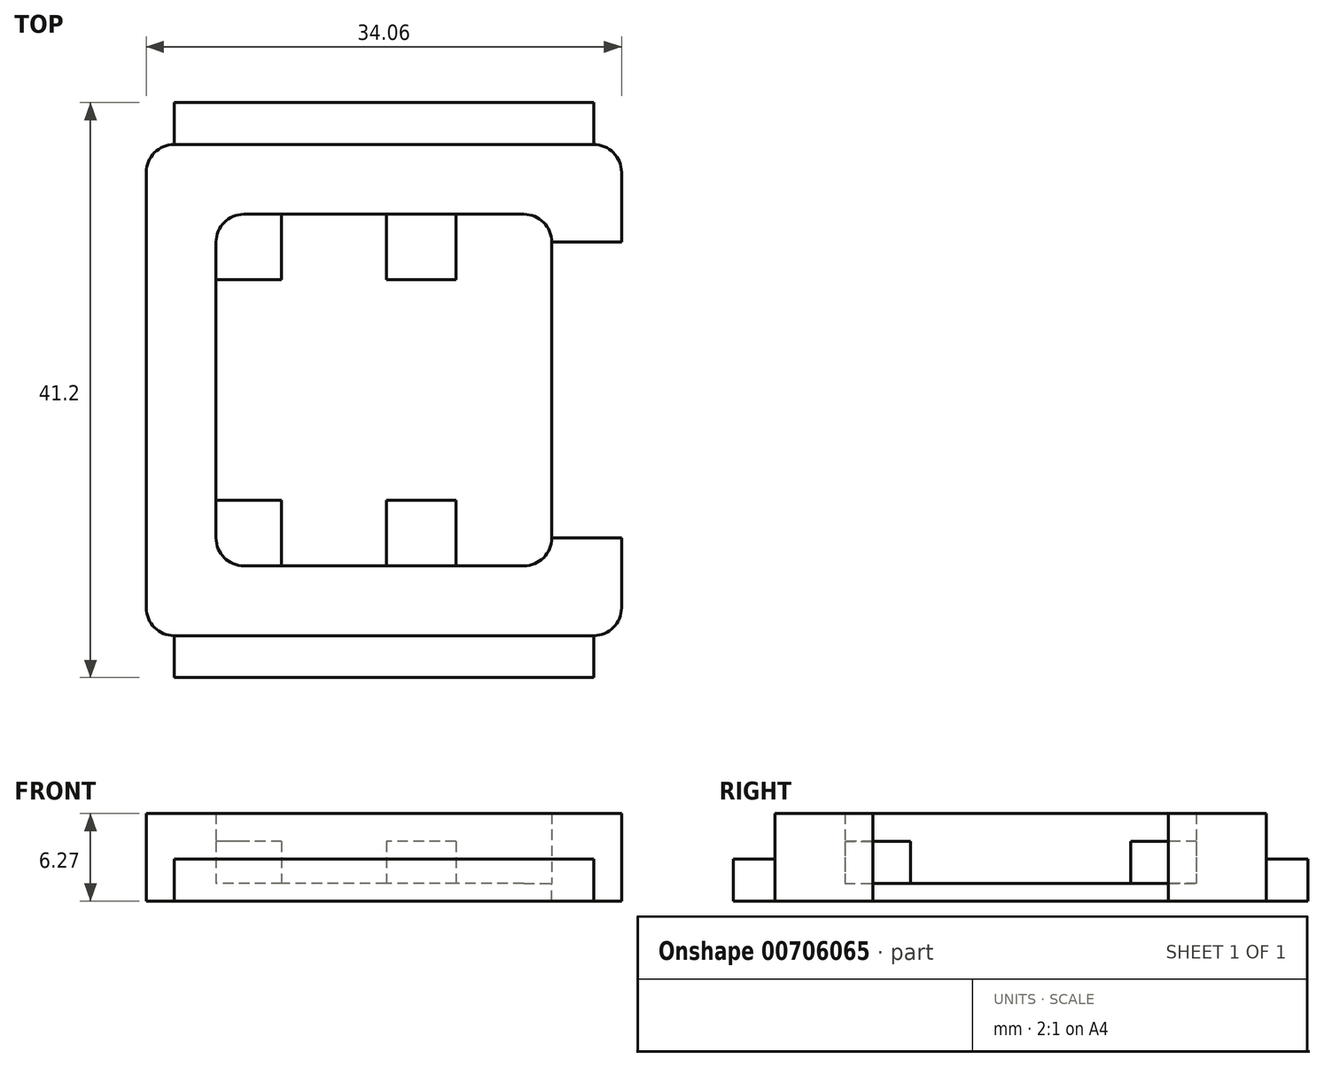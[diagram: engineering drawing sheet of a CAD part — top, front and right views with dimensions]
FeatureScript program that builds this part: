
annotation { "Feature Type Name" : "Feature", "Feature Type Description" : "" }
export const myFeature = defineFeature(function(context is Context, id is Id, definition is map)
    precondition{}
    {
        {
            var Q0;
            Q0=qCreatedBy(makeId("Top.planeOp"),FACE);
            var sketch = newSketch(context, id + "F0", { "sketchPlane" : qUnion([Q0])});
            skLineSegment(sketch, "E0.bottom", {"start": v(10.03, -12.6) * mm, "end": v(-10.03, -12.6) * mm});
            skLineSegment(sketch, "E0.top", {"start": v(10.03, 12.6) * mm, "end": v(-10.03, 12.6) * mm});
            skLineSegment(sketch, "E0.left", {"start": v(12.03, -10.6) * mm, "end": v(12.03, 10.6) * mm});
            skLineSegment(sketch, "E0.right", {"start": v(-12.03, -10.6) * mm, "end": v(-12.03, 10.6) * mm});
            skPoint(sketch, "E0.middle", {"position": v(0, 0) * mm});
            skPoint(sketch, "E1.visualSharp", {"position": v(-12.03, 12.6) * mm});
            skArc(sketch, "E1.filletArc", {"start": v(-10.03, 12.6) * mm, "mid": v(-11.45, 12.01) * mm, "end": v(-12.03, 10.6) * mm});
            skPoint(sketch, "E2.visualSharp", {"position": v(12.03, 12.6) * mm});
            skArc(sketch, "E2.filletArc", {"start": v(12.03, 10.6) * mm, "mid": v(11.45, 12.01) * mm, "end": v(10.03, 12.6) * mm});
            skPoint(sketch, "E3.visualSharp", {"position": v(12.03, -12.6) * mm});
            skArc(sketch, "E3.filletArc", {"start": v(10.03, -12.6) * mm, "mid": v(11.45, -12.01) * mm, "end": v(12.03, -10.6) * mm});
            skPoint(sketch, "E4.visualSharp", {"position": v(-12.03, -12.6) * mm});
            skArc(sketch, "E4.filletArc", {"start": v(-12.03, -10.6) * mm, "mid": v(-11.45, -12.01) * mm, "end": v(-10.03, -12.6) * mm});
            skCircle(sketch, "E5", {"center": v(-10.03, -10.6) * mm, "radius": 1.1 * mm, "construction": true});
            skCircle(sketch, "E6", {"center": v(-10.03, 10.6) * mm, "radius": 1.1 * mm, "construction": true});
            skLineSegment(sketch, "E7", {"start": v(-12.03, 10.6) * mm, "end": v(2.67, 10.6) * mm, "construction": true});
            skCircle(sketch, "E8", {"center": v(2.67, 10.6) * mm, "radius": 1.1 * mm, "construction": true});
            skCircle(sketch, "E9", {"center": v(2.67, -10.6) * mm, "radius": 1.1 * mm, "construction": true});
            skLineSegment(sketch, "E10.bottom", {"start": v(12.03, 10.4) * mm, "end": v(6.33, 10.4) * mm, "construction": true});
            skLineSegment(sketch, "E10.top", {"start": v(12.03, -10.4) * mm, "end": v(6.33, -10.4) * mm, "construction": true});
            skLineSegment(sketch, "E10.left", {"start": v(12.03, 10.4) * mm, "end": v(12.03, -10.4) * mm});
            skLineSegment(sketch, "E10.right", {"start": v(6.33, 10.4) * mm, "end": v(6.33, -10.4) * mm, "construction": true});
            skPoint(sketch, "E11", {"position": v(6.33, 0) * mm});
            skLineSegment(sketch, "E12", {"start": v(-7.33, -12.6) * mm, "end": v(-7.33, -7.9) * mm});
            skLineSegment(sketch, "E13", {"start": v(-7.33, -7.9) * mm, "end": v(-12.03, -7.9) * mm});
            skLineSegment(sketch, "E14", {"start": v(-7.33, 12.6) * mm, "end": v(-7.33, 7.9) * mm});
            skLineSegment(sketch, "E15", {"start": v(-7.33, 7.9) * mm, "end": v(-12.03, 7.9) * mm});
            skLineSegment(sketch, "E16.bottom", {"start": v(5.17, 12.6) * mm, "end": v(0.17, 12.6) * mm});
            skLineSegment(sketch, "E16.top", {"start": v(5.17, 7.9) * mm, "end": v(0.17, 7.9) * mm});
            skLineSegment(sketch, "E16.left", {"start": v(5.17, 12.6) * mm, "end": v(5.17, 7.9) * mm});
            skLineSegment(sketch, "E16.right", {"start": v(0.17, 12.6) * mm, "end": v(0.17, 7.9) * mm});
            skPoint(sketch, "E17", {"position": v(2.67, 7.9) * mm});
            skLineSegment(sketch, "E18.bottom", {"start": v(5.17, -12.6) * mm, "end": v(0.17, -12.6) * mm});
            skLineSegment(sketch, "E18.top", {"start": v(5.17, -7.9) * mm, "end": v(0.17, -7.9) * mm});
            skLineSegment(sketch, "E18.left", {"start": v(5.17, -12.6) * mm, "end": v(5.17, -7.9) * mm});
            skLineSegment(sketch, "E18.right", {"start": v(0.17, -12.6) * mm, "end": v(0.17, -7.9) * mm});
            skLineSegment(sketch, "E19.bottom", {"start": v(-15.03, 17.6) * mm, "end": v(15.03, 17.6) * mm});
            skLineSegment(sketch, "E19.top", {"start": v(-15.03, -17.6) * mm, "end": v(15.03, -17.6) * mm});
            skLineSegment(sketch, "E19.left", {"start": v(-17.03, 15.6) * mm, "end": v(-17.03, -15.6) * mm});
            skLineSegment(sketch, "E19.right", {"start": v(17.03, 15.6) * mm, "end": v(17.03, -15.6) * mm});
            skPoint(sketch, "E20.visualSharp", {"position": v(-17.03, -17.6) * mm});
            skArc(sketch, "E20.filletArc", {"start": v(-17.03, -15.6) * mm, "mid": v(-16.45, -17.01) * mm, "end": v(-15.03, -17.6) * mm});
            skPoint(sketch, "E21.visualSharp", {"position": v(17.03, -17.6) * mm});
            skArc(sketch, "E21.filletArc", {"start": v(15.03, -17.6) * mm, "mid": v(16.45, -17.01) * mm, "end": v(17.03, -15.6) * mm});
            skPoint(sketch, "E22.visualSharp", {"position": v(-17.03, 17.6) * mm});
            skArc(sketch, "E22.filletArc", {"start": v(-15.03, 17.6) * mm, "mid": v(-16.45, 17.01) * mm, "end": v(-17.03, 15.6) * mm});
            skPoint(sketch, "E23.visualSharp", {"position": v(17.03, 17.6) * mm});
            skArc(sketch, "E23.filletArc", {"start": v(17.03, 15.6) * mm, "mid": v(16.45, 17.01) * mm, "end": v(15.03, 17.6) * mm});
            skLineSegment(sketch, "E24", {"start": v(12.03, -10.6) * mm, "end": v(17.03, -10.6) * mm});
            skLineSegment(sketch, "E25", {"start": v(12.03, 10.6) * mm, "end": v(17.03, 10.6) * mm});
            skSolve(sketch);
        }
        {
            var Q0;
            {var subQ8=sQuery(id+"F0.wireOp",EDGE,"E1.filletArc");Q0=makeQuery(id+"F0.imprint","IMPRINT",FACE,{"disambiguationData":[TD([[makeQuery(id+"F0.imprint","IMPRINT",EDGE,{"derivedFrom":subQ8}),-1.0]])]});}
            var Q1;
            {var subQ3=sQuery(id+"F0.wireOp",EDGE,"E2.filletArc");Q1=makeQuery(id+"F0.imprint","IMPRINT",FACE,{"disambiguationData":[TD([[makeQuery(id+"F0.imprint","IMPRINT",EDGE,{"derivedFrom":subQ3}),1.0]])]});}
            var Q2;
            {var subQ1=sQuery(id+"F0.wireOp",EDGE,"E1.filletArc");Q2=makeQuery(id+"F0.imprint","IMPRINT",FACE,{"disambiguationData":[TD([[makeQuery(id+"F0.imprint","IMPRINT",EDGE,{"derivedFrom":subQ1}),1.0]])]});}
            var Q3;
            Q3=makeQuery(id+"F0.imprint","IMPRINT",FACE,{"disambiguationData":[TD([[makeQuery(id+"F0.imprint","IMPRINT",EDGE,{"derivedFrom":sQuery(id+"F0.wireOp",EDGE,"E16.top")}),-1.0]])]});
            var Q4;
            Q4=makeQuery(id+"F0.imprint","IMPRINT",FACE,{"disambiguationData":[TD([[makeQuery(id+"F0.imprint","IMPRINT",EDGE,{"derivedFrom":sQuery(id+"F0.wireOp",EDGE,"E18.top")}),1.0]])]});
            var Q5;
            {var subQ0=sQuery(id+"F0.wireOp",EDGE,"E4.filletArc");Q5=makeQuery(id+"F0.imprint","IMPRINT",FACE,{"disambiguationData":[TD([[makeQuery(id+"F0.imprint","IMPRINT",EDGE,{"derivedFrom":subQ0}),1.0]])]});}
            extrude(context, id + "F1", {"entities" : qUnion([Q0, Q1, Q2, Q3, Q4, Q5]), "oppositeDirection" : true, "depth" : 1.27 * mm, "offsetDistance" : 25 * mm});
        }
        {
            var Q0;
            {var subQ8=sQuery(id+"F0.wireOp",EDGE,"E1.filletArc");Q0=makeQuery(id+"F0.imprint","IMPRINT",FACE,{"disambiguationData":[TD([[makeQuery(id+"F0.imprint","IMPRINT",EDGE,{"derivedFrom":subQ8}),-1.0]])]});}
            var Q1;
            {var subQ1=sQuery(id+"F0.wireOp",EDGE,"E1.filletArc");Q1=makeQuery(id+"F0.imprint","IMPRINT",FACE,{"disambiguationData":[TD([[makeQuery(id+"F0.imprint","IMPRINT",EDGE,{"derivedFrom":subQ1}),1.0]])]});}
            var Q2;
            Q2=makeQuery(id+"F0.imprint","IMPRINT",FACE,{"disambiguationData":[TD([[makeQuery(id+"F0.imprint","IMPRINT",EDGE,{"derivedFrom":sQuery(id+"F0.wireOp",EDGE,"E16.top")}),-1.0]])]});
            var Q3;
            Q3=makeQuery(id+"F0.imprint","IMPRINT",FACE,{"disambiguationData":[TD([[makeQuery(id+"F0.imprint","IMPRINT",EDGE,{"derivedFrom":sQuery(id+"F0.wireOp",EDGE,"E18.top")}),1.0]])]});
            var Q4;
            {var subQ0=sQuery(id+"F0.wireOp",EDGE,"E4.filletArc");Q4=makeQuery(id+"F0.imprint","IMPRINT",FACE,{"disambiguationData":[TD([[makeQuery(id+"F0.imprint","IMPRINT",EDGE,{"derivedFrom":subQ0}),1.0]])]});}
            extrude(context, id + "F2", {"entities" : qUnion([Q0, Q1, Q2, Q3, Q4]), "operationType" : NewBodyOperationType.ADD, "depth" : 3 * mm, "offsetDistance" : 25 * mm});
        }
        {
            var Q0;
            Q0=makeQuery(id+"F2.opExtrude","CAP_FACE",FACE,{"disambiguationData":[OSD([sQuery(id+"F0.wireOp",EDGE,"E0.bottom"),sQuery(id+"F0.wireOp",EDGE,"E0.top"),sQuery(id+"F0.wireOp",EDGE,"E0.right"),sQuery(id+"F0.wireOp",EDGE,"E2.filletArc"),sQuery(id+"F0.wireOp",EDGE,"E3.filletArc"),sQuery(id+"F0.wireOp",EDGE,"E12"),sQuery(id+"F0.wireOp",EDGE,"E13"),sQuery(id+"F0.wireOp",EDGE,"E14"),sQuery(id+"F0.wireOp",EDGE,"E15"),sQuery(id+"F0.wireOp",EDGE,"E16.top"),sQuery(id+"F0.wireOp",EDGE,"E16.left"),sQuery(id+"F0.wireOp",EDGE,"E16.right"),sQuery(id+"F0.wireOp",EDGE,"E18.top"),sQuery(id+"F0.wireOp",EDGE,"E18.left"),sQuery(id+"F0.wireOp",EDGE,"E18.right"),sQuery(id+"F0.wireOp",EDGE,"E19.bottom"),sQuery(id+"F0.wireOp",EDGE,"E19.top"),sQuery(id+"F0.wireOp",EDGE,"E19.left"),sQuery(id+"F0.wireOp",EDGE,"E19.right"),sQuery(id+"F0.wireOp",EDGE,"E20.filletArc"),sQuery(id+"F0.wireOp",EDGE,"E21.filletArc"),sQuery(id+"F0.wireOp",EDGE,"E22.filletArc"),sQuery(id+"F0.wireOp",EDGE,"E23.filletArc"),sQuery(id+"F0.wireOp",EDGE,"E24"),sQuery(id+"F0.wireOp",EDGE,"E25")])],"isStart":false});
            var sketch = newSketch(context, id + "F3", { "sketchPlane" : qUnion([Q0])});
            skLineSegment(sketch, "E26.bottom", {"start": v(-10.03, 12.6) * mm, "end": v(10.03, 12.6) * mm});
            skLineSegment(sketch, "E26.top", {"start": v(-10.03, -12.6) * mm, "end": v(10.03, -12.6) * mm});
            skLineSegment(sketch, "E26.left", {"start": v(-12.03, 10.6) * mm, "end": v(-12.03, -10.6) * mm});
            skLineSegment(sketch, "E26.right", {"start": v(12.03, 10.6) * mm, "end": v(12.03, -10.6) * mm});
            skPoint(sketch, "E26.middle", {"position": v(0, 0) * mm});
            skPoint(sketch, "E27.visualSharp", {"position": v(-12.03, -12.6) * mm});
            skArc(sketch, "E27.filletArc", {"start": v(-12.03, -10.6) * mm, "mid": v(-11.45, -12.01) * mm, "end": v(-10.03, -12.6) * mm});
            skPoint(sketch, "E28.visualSharp", {"position": v(-12.03, 12.6) * mm});
            skArc(sketch, "E28.filletArc", {"start": v(-10.03, 12.6) * mm, "mid": v(-11.45, 12.01) * mm, "end": v(-12.03, 10.6) * mm});
            skPoint(sketch, "E29.visualSharp", {"position": v(12.03, 12.6) * mm});
            skArc(sketch, "E29.filletArc", {"start": v(12.03, 10.6) * mm, "mid": v(11.45, 12.01) * mm, "end": v(10.03, 12.6) * mm});
            skPoint(sketch, "E30.visualSharp", {"position": v(12.03, -12.6) * mm});
            skArc(sketch, "E30.filletArc", {"start": v(10.03, -12.6) * mm, "mid": v(11.45, -12.01) * mm, "end": v(12.03, -10.6) * mm});
            skSolve(sketch);
        }
        {
            var Q0;
            {var subQ3=sQuery(id+"F3.wireOp",EDGE,"E27.filletArc");Q0=makeQuery(id+"F3.imprint","IMPRINT",FACE,{"disambiguationData":[TD([[makeQuery(id+"F3.imprint","IMPRINT",EDGE,{"derivedFrom":subQ3}),-1.0]])]});}
            extrude(context, id + "F4", {"entities" : qUnion([Q0]), "operationType" : NewBodyOperationType.ADD, "depth" : 2 * mm, "offsetDistance" : 25 * mm});
        }
        {
            var Q0;
            {var subQ0=sQuery(id+"F0.wireOp",EDGE,"E19.bottom");Q0=makeQuery(id+"F4.boolean.opBoolean","MERGE",FACE,{"derivedFrom":[makeQuery(id+"F2.boolean.opBoolean","MERGE",FACE,{"derivedFrom":[makeQuery(id+"F1.opExtrude","SWEPT_FACE",FACE,{"disambiguationData":[OSD([subQ0])]}),makeQuery(id+"F2.opExtrude","SWEPT_FACE",FACE,{"disambiguationData":[OSD([subQ0])]})]}),makeQuery(id+"F4.opExtrude","SWEPT_FACE",FACE,{"disambiguationData":[OSD([subQ0])]})]});}
            var sketch = newSketch(context, id + "F5", { "sketchPlane" : qUnion([Q0])});
            skLineSegment(sketch, "E31", {"start": v(-15.03, 1.73) * mm, "end": v(15.03, 1.73) * mm});
            skSolve(sketch);
        }
        {
            var Q0;
            Q0 = qSketchRegion(id + "F5", true);
            var Q1;
            {var subQ0=sQuery(id+"F5.wireOp",EDGE,"E31");Q1=makeQuery(id+"F5.imprint","IMPRINT",FACE,{"disambiguationData":[TD([[makeQuery(id+"F5.imprint","IMPRINT",EDGE,{"derivedFrom":subQ0}),-1.0]])]});}
            extrude(context, id + "F6", {"entities" : qUnion([Q0, Q1]), "operationType" : NewBodyOperationType.ADD, "depth" : 3 * mm, "offsetDistance" : 25 * mm});
        }
        {
            var Q0;
            {var subQ0=sQuery(id+"F0.wireOp",EDGE,"E19.top");Q0=makeQuery(id+"F4.boolean.opBoolean","MERGE",FACE,{"derivedFrom":[makeQuery(id+"F2.boolean.opBoolean","MERGE",FACE,{"derivedFrom":[makeQuery(id+"F1.opExtrude","SWEPT_FACE",FACE,{"disambiguationData":[OSD([subQ0])]}),makeQuery(id+"F2.opExtrude","SWEPT_FACE",FACE,{"disambiguationData":[OSD([subQ0])]})]}),makeQuery(id+"F4.opExtrude","SWEPT_FACE",FACE,{"disambiguationData":[OSD([subQ0])]})]});}
            var sketch = newSketch(context, id + "F7", { "sketchPlane" : qUnion([Q0])});
            skLineSegment(sketch, "E32", {"start": v(-15.03, 1.73) * mm, "end": v(15.03, 1.73) * mm});
            skSolve(sketch);
        }
        {
            var Q0;
            {var subQ0=sQuery(id+"F7.wireOp",EDGE,"E32");Q0=makeQuery(id+"F7.imprint","IMPRINT",FACE,{"disambiguationData":[TD([[makeQuery(id+"F7.imprint","IMPRINT",EDGE,{"derivedFrom":subQ0}),-1.0]])]});}
            extrude(context, id + "F8", {"entities" : qUnion([Q0]), "operationType" : NewBodyOperationType.ADD, "depth" : 3 * mm, "offsetDistance" : 25 * mm});
        }
    });
